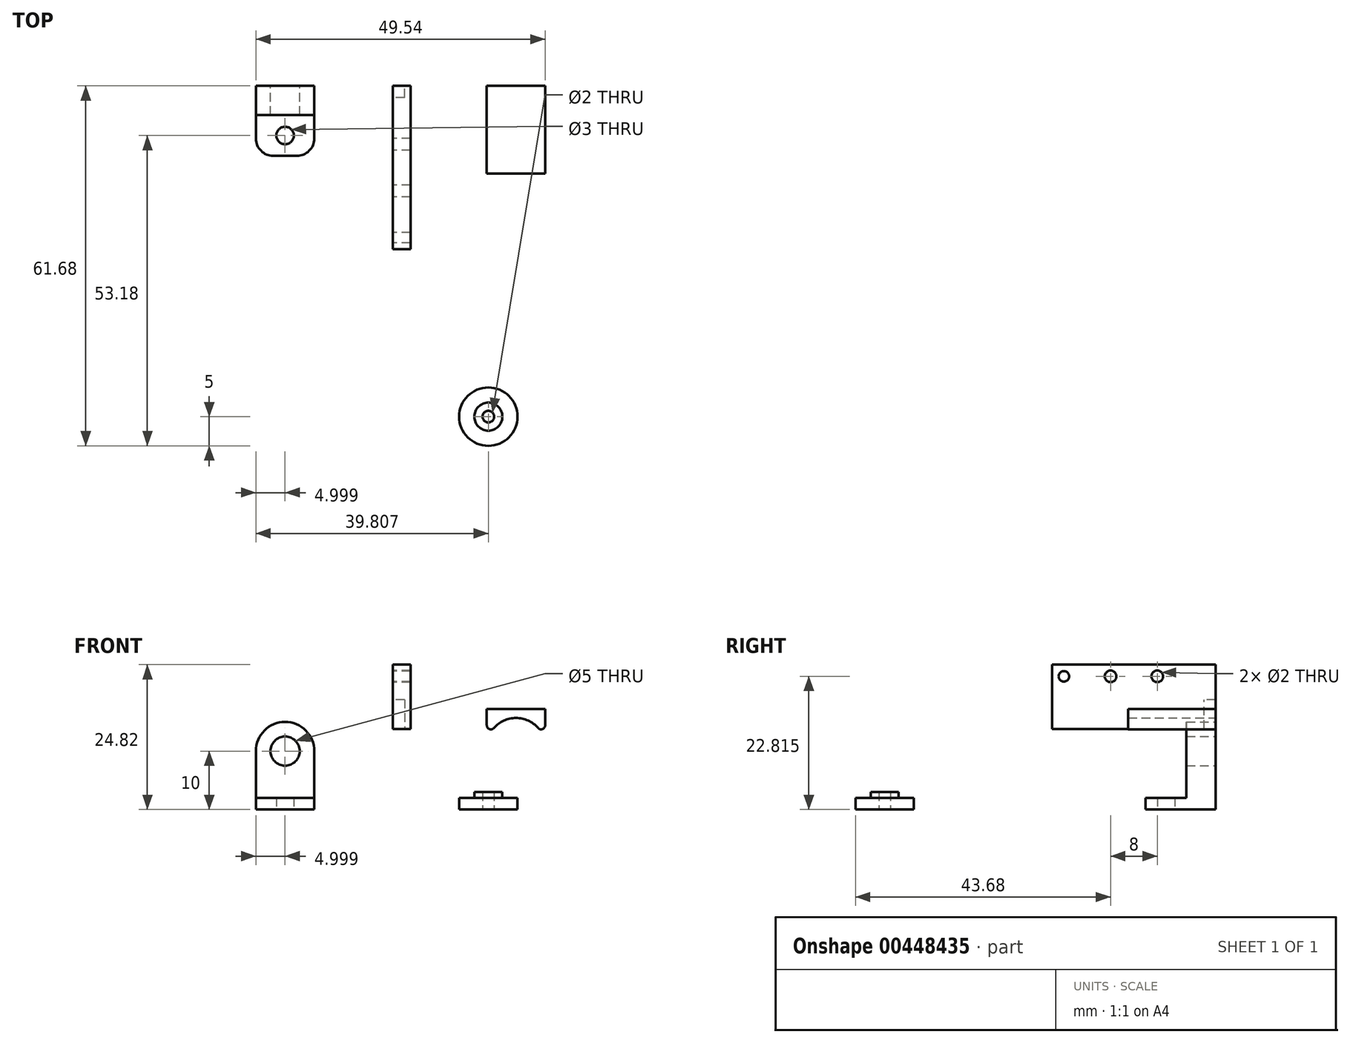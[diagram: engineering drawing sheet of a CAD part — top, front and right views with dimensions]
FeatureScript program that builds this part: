
annotation { "Feature Type Name" : "Feature", "Feature Type Description" : "" }
export const myFeature = defineFeature(function(context is Context, id is Id, definition is map)
    precondition{}
    {
        {
            var Q0;
            Q0=qCreatedBy(makeId("Front.planeOp"),FACE);
            var sketch = newSketch(context, id + "F0", { "sketchPlane" : qUnion([Q0])});
            skCircle(sketch, "E0", {"center": v(13.22, 10) * mm, "radius": 5 * mm});
            skCircle(sketch, "E1", {"center": v(13.22, 10) * mm, "radius": 2.5 * mm});
            skLineSegment(sketch, "E2", {"start": v(8.22, 10) * mm, "end": v(8.22, 0) * mm});
            skLineSegment(sketch, "E3", {"start": v(8.22, 0) * mm, "end": v(18.22, 0) * mm});
            skLineSegment(sketch, "E4", {"start": v(18.22, 0) * mm, "end": v(18.22, 10) * mm});
            skSolve(sketch);
        }
        {
            var Q0;
            Q0=makeQuery(id+"F0.imprint","IMPRINT",FACE,{"disambiguationData":[TD([[makeQuery(id+"F0.imprint","IMPRINT",EDGE,{"derivedFrom":sQuery(id+"F0.wireOp",EDGE,"E1")}),-1.0]])]});
            var Q1;
            {var subQ0=sQuery(id+"F0.wireOp",EDGE,"E2");Q1=makeQuery(id+"F0.imprint","IMPRINT",FACE,{"disambiguationData":[TD([[makeQuery(id+"F0.imprint","IMPRINT",EDGE,{"derivedFrom":subQ0}),1.0]])]});}
            extrude(context, id + "F1", {"entities" : qUnion([Q0, Q1]), "depth" : 5 * mm});
        }
        {
            var Q0;
            Q0=makeQuery(id+"F1.opExtrude","SWEPT_FACE",FACE,{"disambiguationData":[OSD([sQuery(id+"F0.wireOp",EDGE,"E3")])]});
            var sketch = newSketch(context, id + "F2", { "sketchPlane" : qUnion([Q0])});
            skLineSegment(sketch, "E5.bottom", {"start": v(8.22, 5) * mm, "end": v(18.22, 5) * mm});
            skLineSegment(sketch, "E5.top", {"start": v(8.22, 12) * mm, "end": v(18.22, 12) * mm});
            skLineSegment(sketch, "E5.left", {"start": v(8.22, 5) * mm, "end": v(8.22, 12) * mm});
            skLineSegment(sketch, "E5.right", {"start": v(18.22, 5) * mm, "end": v(18.22, 12) * mm});
            skPoint(sketch, "E6", {"position": v(13.22, 8.5) * mm});
            skPoint(sketch, "E6.positionSnap0", {"position": v(8.22, 8.5) * mm});
            skPoint(sketch, "E6.positionSnap1", {"position": v(13.22, 12) * mm});
            skSolve(sketch);
        }
        {
            var Q0;
            Q0=makeQuery(id+"F2.imprint","IMPRINT",FACE,{"disambiguationData":[TD([[makeQuery(id+"F2.imprint","IMPRINT",EDGE,{"derivedFrom":sQuery(id+"F2.wireOp",EDGE,"E5.bottom")}),1.0]])]});
            extrude(context, id + "F3", {"entities" : qUnion([Q0]), "operationType" : NewBodyOperationType.ADD, "oppositeDirection" : true, "depth" : 2 * mm});
        }
        {
            var Q0;
            Q0=sQuery(id+"F2.wireOp",VERTEX,"E6");
            var Q1;
            Q1=makeQuery(id+"F1.opExtrude","SWEPT_BODY",BODY,{"disambiguationData":[OSD([sQuery(id+"F0.wireOp",EDGE,"E0"),sQuery(id+"F0.wireOp",EDGE,"E1"),sQuery(id+"F0.wireOp",EDGE,"E2"),sQuery(id+"F0.wireOp",EDGE,"E3"),sQuery(id+"F0.wireOp",EDGE,"E4")])]});
            hole(context, id + "F4", {"style" : HoleStyle.SIMPLE, "endStyle" : HoleEndStyle.THROUGH, "holeDiameter" : 3 * mm, "isTappedThrough" : true, "tappedDepth" : 12 * mm, "tapClearance" : 3, "locations" : qUnion([Q0]), "scope" : qUnion([Q1])});
        }
        {
            var Q0;
            Q0=makeQuery(id+"F3.opExtrude","SWEPT_EDGE",EDGE,{"disambiguationData":[OSD([sQuery(id+"F2.wireOp",EDGE,"E5.top"),sQuery(id+"F2.wireOp",EDGE,"E5.right")])]});
            var Q1;
            Q1=makeQuery(id+"F3.opExtrude","SWEPT_EDGE",EDGE,{"disambiguationData":[OSD([sQuery(id+"F2.wireOp",EDGE,"E5.top"),sQuery(id+"F2.wireOp",EDGE,"E5.left")])]});
            fillet(context, id + "F5", {"entities" : qUnion([Q0, Q1]), "radius" : 3 * mm, "tangentPropagation" : true, "allowEdgeOverflow" : false});
        }
        {
            var Q0;
            Q0=qCreatedBy(makeId("Front.planeOp"),FACE);
            var sketch = newSketch(context, id + "F6", { "sketchPlane" : qUnion([Q0])});
            skLineSegment(sketch, "E7.bottom", {"start": v(31.68, 24.82) * mm, "end": v(34.68, 24.82) * mm});
            skLineSegment(sketch, "E7.top", {"start": v(31.68, 13.82) * mm, "end": v(34.68, 13.82) * mm});
            skLineSegment(sketch, "E7.left", {"start": v(31.68, 24.82) * mm, "end": v(31.68, 13.82) * mm});
            skLineSegment(sketch, "E7.right", {"start": v(34.68, 24.82) * mm, "end": v(34.68, 13.82) * mm});
            skSolve(sketch);
        }
        {
            var Q0;
            Q0=makeQuery(id+"F6.imprint","IMPRINT",FACE,{"disambiguationData":[TD([[makeQuery(id+"F6.imprint","IMPRINT",EDGE,{"derivedFrom":sQuery(id+"F6.wireOp",EDGE,"E7.bottom")}),-1.0]])]});
            extrude(context, id + "F7", {"entities" : qUnion([Q0]), "depth" : 28 * mm});
        }
        {
            var Q0;
            Q0=makeQuery(id+"F7.opExtrude","SWEPT_FACE",FACE,{"disambiguationData":[OSD([sQuery(id+"F6.wireOp",EDGE,"E7.left")])]});
            var sketch = newSketch(context, id + "F8", { "sketchPlane" : qUnion([Q0])});
            skPoint(sketch, "E8", {"position": v(18, 22.82) * mm});
            skPoint(sketch, "E9", {"position": v(10, 22.82) * mm});
            skPoint(sketch, "E10", {"position": v(26, 22.82) * mm});
            skLineSegment(sketch, "E11.bottom", {"start": v(0, 13.82) * mm, "end": v(2, 13.82) * mm});
            skLineSegment(sketch, "E11.top", {"start": v(0, 18.82) * mm, "end": v(2, 18.82) * mm});
            skLineSegment(sketch, "E11.left", {"start": v(0, 13.82) * mm, "end": v(0, 18.82) * mm});
            skLineSegment(sketch, "E11.right", {"start": v(2, 13.82) * mm, "end": v(2, 18.82) * mm});
            skSolve(sketch);
        }
        {
            var Q0;
            Q0=makeQuery(id+"F8.imprint","IMPRINT",FACE,{"disambiguationData":[TD([[makeQuery(id+"F8.imprint","IMPRINT",EDGE,{"derivedFrom":sQuery(id+"F8.wireOp",EDGE,"E11.bottom")}),-1.0]])]});
            extrude(context, id + "F9", {"entities" : qUnion([Q0]), "operationType" : NewBodyOperationType.REMOVE, "oppositeDirection" : true, "depth" : 2 * mm});
        }
        {
            var Q0;
            Q0=sQuery(id+"F8.wireOp",VERTEX,"E9");
            var Q1;
            Q1=sQuery(id+"F8.wireOp",VERTEX,"E8");
            var Q2;
            Q2=makeQuery(id+"F7.opExtrude","SWEPT_BODY",BODY,{"disambiguationData":[OSD([sQuery(id+"F6.wireOp",EDGE,"E7.bottom"),sQuery(id+"F6.wireOp",EDGE,"E7.top"),sQuery(id+"F6.wireOp",EDGE,"E7.left"),sQuery(id+"F6.wireOp",EDGE,"E7.right")])]});
            hole(context, id + "F10", {"style" : HoleStyle.SIMPLE, "endStyle" : HoleEndStyle.THROUGH, "holeDiameter" : 2 * mm, "isTappedThrough" : true, "tappedDepth" : 12 * mm, "tapClearance" : 3, "locations" : qUnion([Q0, Q1]), "scope" : qUnion([Q2])});
        }
        {
            var Q0;
            Q0=sQuery(id+"F8.wireOp",VERTEX,"E10");
            var Q1;
            Q1=makeQuery(id+"F7.opExtrude","SWEPT_BODY",BODY,{"disambiguationData":[OSD([sQuery(id+"F6.wireOp",EDGE,"E7.bottom"),sQuery(id+"F6.wireOp",EDGE,"E7.top"),sQuery(id+"F6.wireOp",EDGE,"E7.left"),sQuery(id+"F6.wireOp",EDGE,"E7.right")])]});
            hole(context, id + "F11", {"style" : HoleStyle.SIMPLE, "endStyle" : HoleEndStyle.THROUGH, "holeDiameter" : 1.8 * mm, "isTappedThrough" : true, "tappedDepth" : 12 * mm, "tapClearance" : 3, "locations" : qUnion([Q0]), "scope" : qUnion([Q1])});
        }
        {
            var Q0;
            Q0=qCreatedBy(makeId("Front.planeOp"),FACE);
            var sketch = newSketch(context, id + "F12", { "sketchPlane" : qUnion([Q0])});
            skLineSegment(sketch, "E12.bottom", {"start": v(47.76, 17.19) * mm, "end": v(57.76, 17.19) * mm});
            skLineSegment(sketch, "E12.top", {"start": v(47.76, 15.69) * mm, "end": v(57.76, 15.69) * mm});
            skLineSegment(sketch, "E12.left", {"start": v(47.76, 17.19) * mm, "end": v(47.76, 15.69) * mm});
            skLineSegment(sketch, "E12.right", {"start": v(57.76, 17.19) * mm, "end": v(57.76, 15.69) * mm});
            skCircle(sketch, "E13", {"center": v(52.76, 10.69) * mm, "radius": 5 * mm});
            skPoint(sketch, "E13.centerSnap0", {"position": v(52.76, 15.69) * mm});
            skLineSegment(sketch, "E14", {"start": v(47.76, 15.69) * mm, "end": v(47.76, 10.69) * mm});
            skLineSegment(sketch, "E15", {"start": v(57.76, 15.69) * mm, "end": v(57.76, 10.69) * mm});
            skSolve(sketch);
        }
        {
            var Q0;
            {var subQ0=sQuery(id+"F12.wireOp",EDGE,"E14");Q0=makeQuery(id+"F12.imprint","IMPRINT",FACE,{"disambiguationData":[TD([[makeQuery(id+"F12.imprint","IMPRINT",EDGE,{"derivedFrom":subQ0}),1.0]])]});}
            var Q1;
            Q1=makeQuery(id+"F12.imprint","IMPRINT",FACE,{"disambiguationData":[TD([[makeQuery(id+"F12.imprint","IMPRINT",EDGE,{"derivedFrom":sQuery(id+"F12.wireOp",EDGE,"E12.bottom")}),-1.0]])]});
            var Q2;
            {var subQ0=sQuery(id+"F12.wireOp",EDGE,"E15");Q2=makeQuery(id+"F12.imprint","IMPRINT",FACE,{"disambiguationData":[TD([[makeQuery(id+"F12.imprint","IMPRINT",EDGE,{"derivedFrom":subQ0}),-1.0]])]});}
            extrude(context, id + "F13", {"entities" : qUnion([Q0, Q1, Q2]), "depth" : 15 * mm});
        }
        {
            var Q0;
            Q0=makeQuery(id+"F13.opExtrude","SWEPT_EDGE",EDGE,{"disambiguationData":[OSD([sQuery(id+"F12.wireOp",EDGE,"E13"),sQuery(id+"F12.wireOp",EDGE,"E14")])]});
            var Q1;
            Q1=makeQuery(id+"F13.opExtrude","SWEPT_EDGE",EDGE,{"disambiguationData":[OSD([sQuery(id+"F12.wireOp",EDGE,"E13"),sQuery(id+"F12.wireOp",EDGE,"E15")])]});
            fillet(context, id + "F14", {"entities" : qUnion([Q0, Q1]), "radius" : 0.7 * mm, "tangentPropagation" : true, "allowEdgeOverflow" : false});
        }
        {
            var Q0;
            Q0=qCreatedBy(makeId("Top.planeOp"),FACE);
            var sketch = newSketch(context, id + "F15", { "sketchPlane" : qUnion([Q0])});
            skCircle(sketch, "E16", {"center": v(48.03, -56.68) * mm, "radius": 5 * mm});
            skSolve(sketch);
        }
        {
            var Q0;
            Q0=makeQuery(id+"F15.imprint","IMPRINT",FACE,{"disambiguationData":[TD([[makeQuery(id+"F15.imprint","IMPRINT",EDGE,{"derivedFrom":sQuery(id+"F15.wireOp",EDGE,"E16")}),1.0]])]});
            extrude(context, id + "F16", {"entities" : qUnion([Q0]), "depth" : 2 * mm});
        }
        {
            var Q0;
            Q0=makeQuery(id+"F16.opExtrude","CAP_FACE",FACE,{"disambiguationData":[OSD([sQuery(id+"F15.wireOp",EDGE,"E16")])],"isStart":false});
            var sketch = newSketch(context, id + "F17", { "sketchPlane" : qUnion([Q0])});
            skCircle(sketch, "E17.0.0", {"center": v(48.03, -56.68) * mm, "radius": 5 * mm});
            skCircle(sketch, "E18", {"center": v(48.03, -56.68) * mm, "radius": 2.4 * mm});
            skSolve(sketch);
        }
        {
            var Q0;
            Q0=makeQuery(id+"F17.imprint","IMPRINT",FACE,{"disambiguationData":[TD([[makeQuery(id+"F17.imprint","IMPRINT",EDGE,{"derivedFrom":sQuery(id+"F17.wireOp",EDGE,"E18")}),1.0]])]});
            extrude(context, id + "F18", {"entities" : qUnion([Q0]), "operationType" : NewBodyOperationType.ADD, "depth" : 1 * mm});
        }
        {
            var Q0;
            Q0=sQuery(id+"F15.wireOp",VERTEX,"E16.center");
            var Q1;
            Q1=makeQuery(id+"F16.opExtrude","SWEPT_BODY",BODY,{"disambiguationData":[OSD([sQuery(id+"F15.wireOp",EDGE,"E16")])]});
            hole(context, id + "F19", {"style" : HoleStyle.SIMPLE, "endStyle" : HoleEndStyle.THROUGH, "oppositeDirection" : true, "holeDiameter" : 2 * mm, "isTappedThrough" : true, "tappedDepth" : 12 * mm, "tapClearance" : 3, "locations" : qUnion([Q0]), "scope" : qUnion([Q1])});
        }
    });
